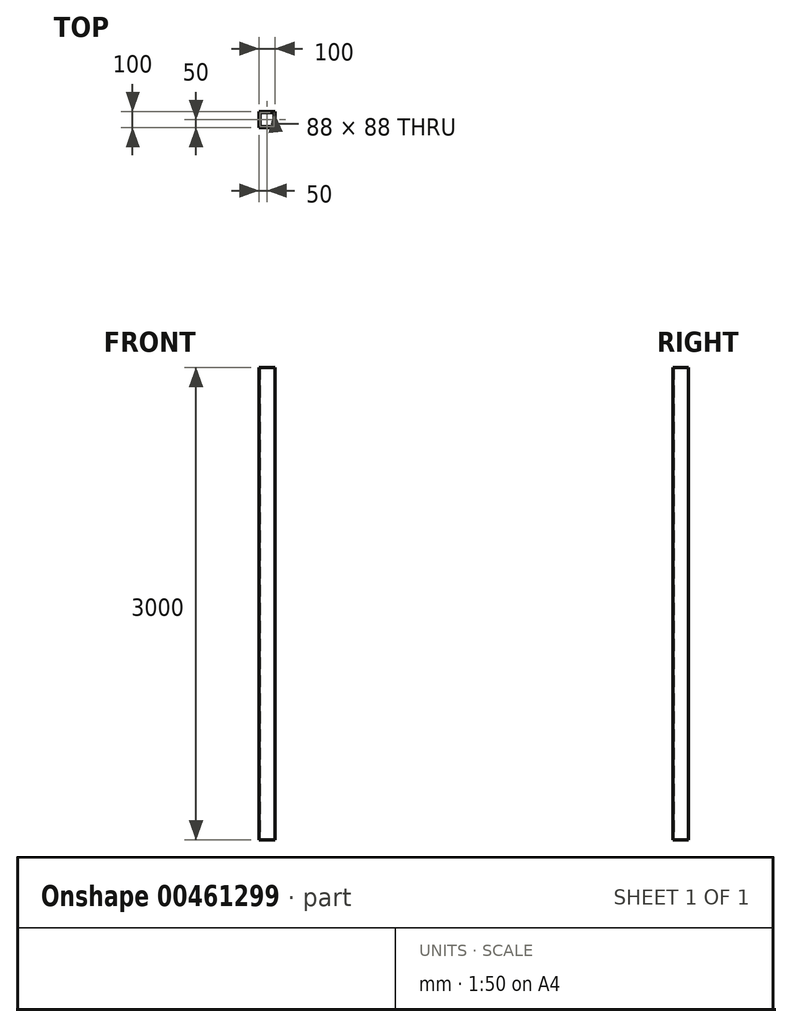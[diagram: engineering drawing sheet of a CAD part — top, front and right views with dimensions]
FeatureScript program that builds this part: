
annotation { "Feature Type Name" : "Feature", "Feature Type Description" : "" }
export const myFeature = defineFeature(function(context is Context, id is Id, definition is map)
    precondition{}
    {
        {
            var Q0;
            Q0=qCreatedBy(makeId("Top.planeOp"),FACE);
            var sketch = newSketch(context, id + "F0", { "sketchPlane" : qUnion([Q0])});
            skLineSegment(sketch, "E0.bottom", {"start": v(50, -50) * mm, "end": v(-50, -50) * mm});
            skLineSegment(sketch, "E0.top", {"start": v(50, 50) * mm, "end": v(-50, 50) * mm});
            skLineSegment(sketch, "E0.left", {"start": v(50, -50) * mm, "end": v(50, 50) * mm});
            skLineSegment(sketch, "E0.right", {"start": v(-50, -50) * mm, "end": v(-50, 50) * mm});
            skPoint(sketch, "E0.middle", {"position": v(0, 0) * mm});
            skLineSegment(sketch, "E1.bottom", {"start": v(44, -44) * mm, "end": v(-44, -44) * mm});
            skLineSegment(sketch, "E1.top", {"start": v(44, 44) * mm, "end": v(-44, 44) * mm});
            skLineSegment(sketch, "E1.left", {"start": v(44, -44) * mm, "end": v(44, 44) * mm});
            skLineSegment(sketch, "E1.right", {"start": v(-44, -44) * mm, "end": v(-44, 44) * mm});
            skSolve(sketch);
        }
        {
            var Q0;
            Q0=makeQuery(id+"F0.imprint","IMPRINT",FACE,{"disambiguationData":[TD([[makeQuery(id+"F0.imprint","IMPRINT",EDGE,{"derivedFrom":sQuery(id+"F0.wireOp",EDGE,"E0.bottom")}),-1.0]])]});
            extrude(context, id + "F1", {"entities" : qUnion([Q0]), "depth" : 3000 * mm});
        }
    });
